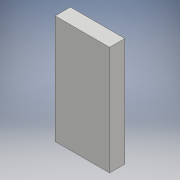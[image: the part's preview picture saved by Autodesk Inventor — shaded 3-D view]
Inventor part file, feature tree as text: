
AUTODESK INVENTOR PART (.ipt)
format: ipt  version: 2017 (Build 210142000, 142)  size: 96,768 bytes
history: native  units: mm
features: extrude x1, sketch x1
ambient origin geometry x8: Origin, YZ Plane, XZ Plane, XY Plane, X Axis, Y Axis, Z Axis, Center Point
bodies: Solid1 (feature_tree)
feature tree (2):
  extrude  "Extrusion1"  Depth=50.0mm
  sketch  "Sketch1"  dims[d0=100.0mm d1=50.0mm d2=14.0mm d3=0.0mm]
